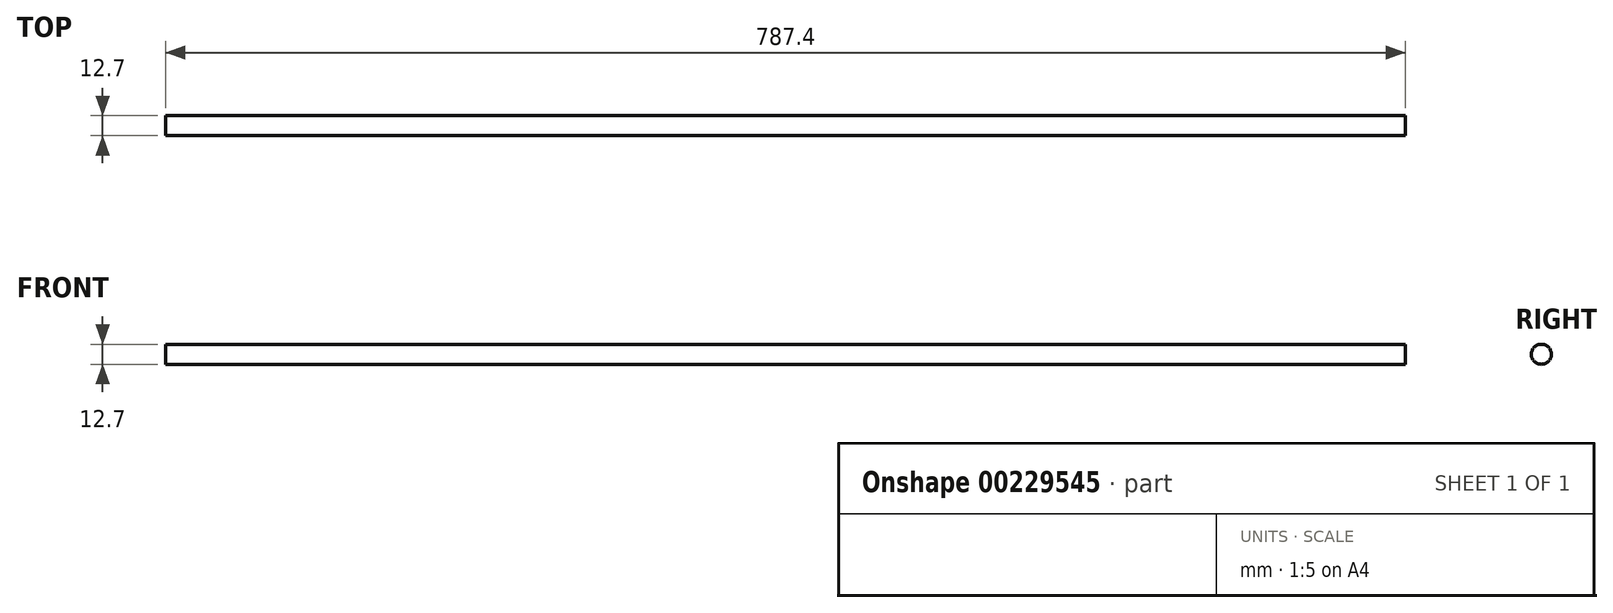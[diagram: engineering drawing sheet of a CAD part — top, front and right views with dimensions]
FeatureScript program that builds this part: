
annotation { "Feature Type Name" : "Feature", "Feature Type Description" : "" }
export const myFeature = defineFeature(function(context is Context, id is Id, definition is map)
    precondition{}
    {
        {
            var Q0;
            Q0=qCreatedBy(makeId("Right.planeOp"),FACE);
            var sketch = newSketch(context, id + "F0", { "sketchPlane" : qUnion([Q0])});
            skCircle(sketch, "E0", {"center": v(0, 0) * mm, "radius": 6.35 * mm});
            skSolve(sketch);
        }
        {
            var Q0;
            Q0 = qSketchRegion(id + "F0", true);
            extrude(context, id + "F1", {"entities" : qUnion([Q0]), "depth" : 393.7 * mm, "hasSecondDirection" : true, "secondDirectionOppositeDirection" : true, "secondDirectionDepth" : 393.7 * mm});
        }
    });
